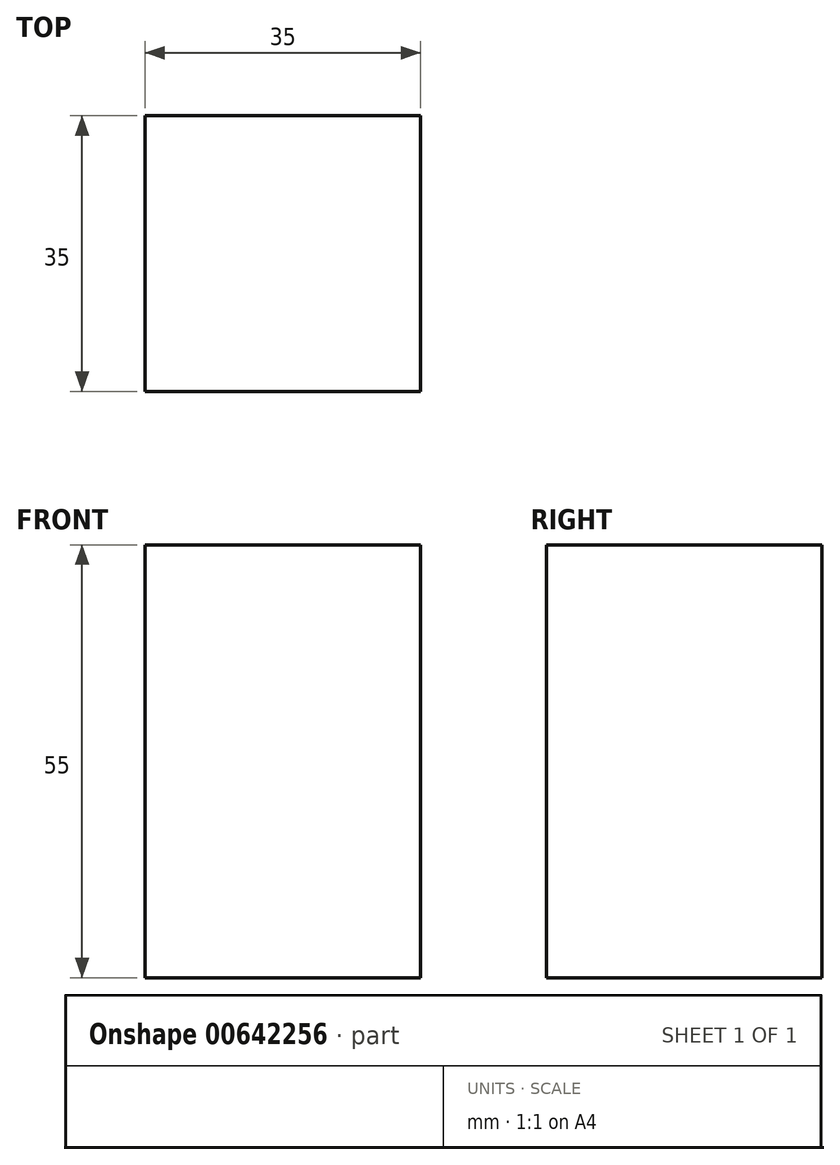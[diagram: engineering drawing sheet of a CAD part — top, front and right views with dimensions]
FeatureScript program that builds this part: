
annotation { "Feature Type Name" : "Feature", "Feature Type Description" : "" }
export const myFeature = defineFeature(function(context is Context, id is Id, definition is map)
    precondition{}
    {
        {
            var Q0;
            Q0=qCreatedBy(makeId("Top.planeOp"),FACE);
            var sketch = newSketch(context, id + "F0", { "sketchPlane" : qUnion([Q0])});
            skLineSegment(sketch, "E0.bottom", {"start": v(-17.5, 17.5) * mm, "end": v(17.5, 17.5) * mm});
            skLineSegment(sketch, "E0.top", {"start": v(-17.5, -17.5) * mm, "end": v(17.5, -17.5) * mm});
            skLineSegment(sketch, "E0.left", {"start": v(-17.5, 17.5) * mm, "end": v(-17.5, -17.5) * mm});
            skLineSegment(sketch, "E0.right", {"start": v(17.5, 17.5) * mm, "end": v(17.5, -17.5) * mm});
            skLineSegment(sketch, "E1", {"start": v(0, 17.5) * mm, "end": v(0, -17.5) * mm, "construction": true});
            skSolve(sketch);
        }
        {
            var Q0;
            Q0=qSketchRegion(id+"F0",true);
            var Q1;
            Q1=qBodyType(qCreatedBy(id+"F0",EDGE),BodyType.WIRE);
            var Q2;
            Q2=sQuery(id+"F0.wireOp",EDGE,"E0.right");
            extrude(context, id + "F1", {"entities" : qUnion([Q0]), "surfaceEntities" : qUnion([Q1, Q2]), "depth" : 55 * mm, "offsetDistance" : 25 * mm});
        }
    });
